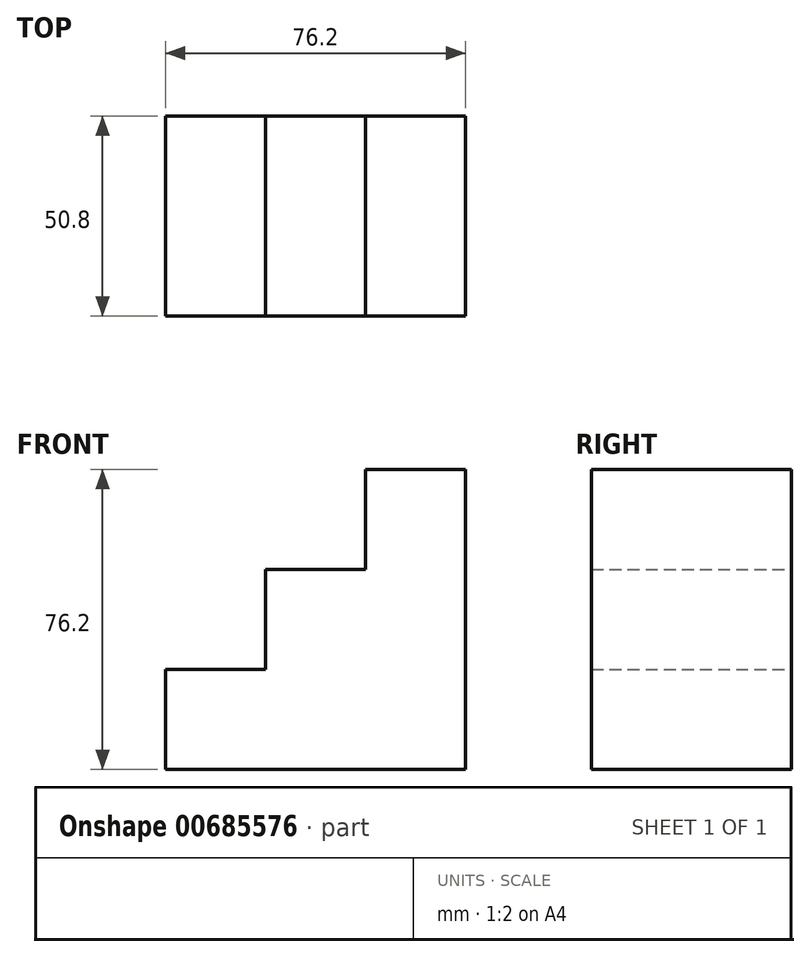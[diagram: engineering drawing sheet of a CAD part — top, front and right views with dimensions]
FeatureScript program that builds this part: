
annotation { "Feature Type Name" : "Feature", "Feature Type Description" : "" }
export const myFeature = defineFeature(function(context is Context, id is Id, definition is map)
    precondition{}
    {
        {
            var Q0;
            Q0=qCreatedBy(makeId("Front.planeOp"),FACE);
            var sketch = newSketch(context, id + "F0", { "sketchPlane" : qUnion([Q0])});
            skLineSegment(sketch, "E0", {"start": v(-49.53, -16.23) * mm, "end": v(-49.53, -41.63) * mm});
            skLineSegment(sketch, "E1", {"start": v(-49.53, -41.63) * mm, "end": v(26.67, -41.63) * mm});
            skLineSegment(sketch, "E2", {"start": v(26.67, -41.63) * mm, "end": v(26.67, 34.57) * mm});
            skLineSegment(sketch, "E3", {"start": v(26.67, 34.57) * mm, "end": v(1.27, 34.57) * mm});
            skLineSegment(sketch, "E4", {"start": v(1.27, 34.57) * mm, "end": v(1.27, 9.17) * mm});
            skLineSegment(sketch, "E5", {"start": v(1.27, 9.17) * mm, "end": v(-24.13, 9.17) * mm});
            skLineSegment(sketch, "E6", {"start": v(-24.13, 9.17) * mm, "end": v(-24.13, -16.23) * mm});
            skLineSegment(sketch, "E7", {"start": v(-24.13, -16.23) * mm, "end": v(-49.53, -16.23) * mm});
            skSolve(sketch);
        }
        {
            var Q0;
            Q0=makeQuery(id+"F0.imprint","IMPRINT",FACE,{"disambiguationData":[TD([[makeQuery(id+"F0.imprint","IMPRINT",EDGE,{"derivedFrom":sQuery(id+"F0.wireOp",EDGE,"E0")}),1.0]])]});
            extrude(context, id + "F1", {"entities" : qUnion([Q0]), "depth" : 50.8 * mm, "offsetDistance" : 25.4 * mm});
        }
    });
